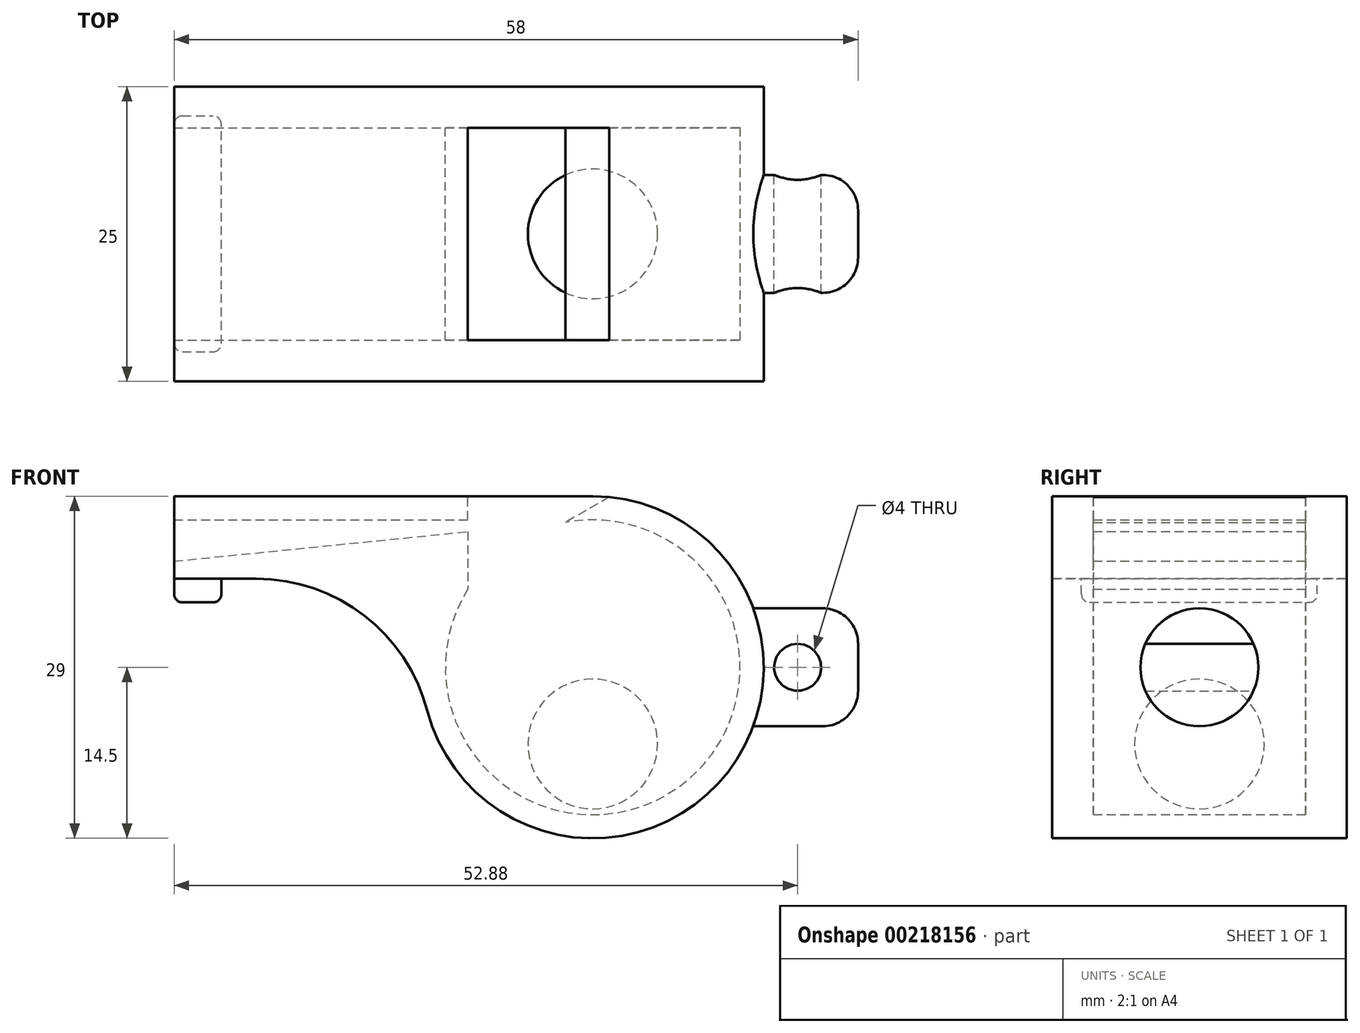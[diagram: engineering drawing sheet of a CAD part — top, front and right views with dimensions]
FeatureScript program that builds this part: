
annotation { "Feature Type Name" : "Feature", "Feature Type Description" : "" }
export const myFeature = defineFeature(function(context is Context, id is Id, definition is map)
    precondition{}
    {
        {
            var Q0;
            Q0=qCreatedBy(makeId("Front.planeOp"),FACE);
            var sketch = newSketch(context, id + "F0", { "sketchPlane" : qUnion([Q0])});
            skLineSegment(sketch, "E0", {"start": v(-35.5, 9) * mm, "end": v(-35.5, 12.5) * mm});
            skLineSegment(sketch, "E1", {"start": v(-35.5, 12.5) * mm, "end": v(-10.59, 12.5) * mm});
            skLineSegment(sketch, "E2", {"start": v(-10.59, 12.5) * mm, "end": v(-10.59, 14.5) * mm});
            skLineSegment(sketch, "E3", {"start": v(-10.59, 14.5) * mm, "end": v(0, 14.5) * mm});
            skLineSegment(sketch, "E4", {"start": v(-35.5, 9) * mm, "end": v(-10.59, 11.5) * mm});
            skLineSegment(sketch, "E5", {"start": v(-10.59, 11.5) * mm, "end": v(-10.59, 6.64) * mm});
            skArc(sketch, "E6", {"start": v(-10.59, 6.64) * mm, "mid": v(7.04, -10.33) * mm, "end": v(-2.3, 12.29) * mm});
            skArc(sketch, "E7", {"start": v(1.41, 14.43) * mm, "mid": v(0.7, 14.48) * mm, "end": v(0, 14.5) * mm});
            skLineSegment(sketch, "E8", {"start": v(-35.5, 9) * mm, "end": v(-1.25, 12.44) * mm, "construction": true});
            skLineSegment(sketch, "E9", {"start": v(1.41, 14.43) * mm, "end": v(-2.3, 12.29) * mm});
            skArc(sketch, "E10", {"start": v(-12.4, 7.5) * mm, "mid": v(7.12, -12.63) * mm, "end": v(0, 14.5) * mm});
            skLineSegment(sketch, "E11.bottom", {"start": v(-35.5, 14.5) * mm, "end": v(0, 14.5) * mm});
            skLineSegment(sketch, "E11.top", {"start": v(-35.5, 7.5) * mm, "end": v(-12.4, 7.5) * mm});
            skLineSegment(sketch, "E11.left", {"start": v(-35.5, 14.5) * mm, "end": v(-35.5, 7.5) * mm});
            skLineSegment(sketch, "E12", {"start": v(-35.5, 12.5) * mm, "end": v(-35.5, 9) * mm});
            skSolve(sketch);
        }
        {
            var Q0;
            {var subQ1=sQuery(id+"F0.wireOp",EDGE,"E4");Q0=makeQuery(id+"F0.imprint","IMPRINT",FACE,{"disambiguationData":[TD([[makeQuery(id+"F0.imprint","IMPRINT",EDGE,{"derivedFrom":subQ1}),-1.0]])]});}
            var Q1;
            {var subQ0=sQuery(id+"F0.wireOp",EDGE,"E1");Q1=makeQuery(id+"F0.imprint","IMPRINT",FACE,{"disambiguationData":[TD([[makeQuery(id+"F0.imprint","IMPRINT",EDGE,{"derivedFrom":subQ0}),1.0]])]});}
            var Q2;
            Q2=makeQuery(id+"F0.imprint","IMPRINT",FACE,{"disambiguationData":[TD([[makeQuery(id+"F0.imprint","IMPRINT",EDGE,{"derivedFrom":sQuery(id+"F0.wireOp",EDGE,"E1")}),-1.0]])]});
            extrude(context, id + "F1", {"entities" : qUnion([Q0, Q1, Q2]), "depth" : 25 * mm, "offsetDistance" : 25 * mm, "symmetric" : true});
        }
        {
            var Q0;
            Q0=makeQuery(id+"F0.imprint","IMPRINT",FACE,{"disambiguationData":[TD([[makeQuery(id+"F0.imprint","IMPRINT",EDGE,{"derivedFrom":sQuery(id+"F0.wireOp",EDGE,"E1")}),-1.0]])]});
            extrude(context, id + "F2", {"entities" : qUnion([Q0]), "operationType" : NewBodyOperationType.REMOVE, "depth" : 18 * mm, "offsetDistance" : 25 * mm, "symmetric" : true});
        }
        {
            var Q0;
            Q0=qCreatedBy(makeId("Front.planeOp"),FACE);
            var sketch = newSketch(context, id + "F3", { "sketchPlane" : qUnion([Q0])});
            skArc(sketch, "E13", {"start": v(0, -1) * mm, "mid": v(-5.5, -6.5) * mm, "end": v(0, -12) * mm});
            skLineSegment(sketch, "E14", {"start": v(0, -1) * mm, "end": v(0, -12) * mm});
            skSolve(sketch);
        }
        {
            var Q0;
            Q0=makeQuery(id+"F3.imprint","IMPRINT",FACE,{"disambiguationData":[TD([[makeQuery(id+"F3.imprint","IMPRINT",EDGE,{"derivedFrom":sQuery(id+"F3.wireOp",EDGE,"E13")}),1.0]])]});
            var Q1;
            Q1=sQuery(id+"F3.wireOp",EDGE,"E14");
            revolve(context, id + "F4", {"entities" : qUnion([Q0]), "axis" : qUnion([Q1]), "revolveType" : RevolveType.FULL});
        }
        {
            var Q0;
            Q0=qCreatedBy(makeId("Front.planeOp"),FACE);
            var sketch = newSketch(context, id + "F5", { "sketchPlane" : qUnion([Q0])});
            skLineSegment(sketch, "E15.bottom", {"start": v(12.5, 5) * mm, "end": v(22.5, 5) * mm});
            skLineSegment(sketch, "E15.top", {"start": v(12.5, 0) * mm, "end": v(22.5, 0) * mm});
            skLineSegment(sketch, "E15.left", {"start": v(12.5, 5) * mm, "end": v(12.5, 0) * mm});
            skLineSegment(sketch, "E15.right", {"start": v(22.5, 5) * mm, "end": v(22.5, 0) * mm});
            skSolve(sketch);
        }
        {
            var Q0;
            Q0=makeQuery(id+"F5.imprint","IMPRINT",FACE,{"disambiguationData":[TD([[makeQuery(id+"F5.imprint","IMPRINT",EDGE,{"derivedFrom":sQuery(id+"F5.wireOp",EDGE,"E15.bottom")}),-1.0]])]});
            var Q1;
            Q1=sQuery(id+"F5.wireOp",EDGE,"E15.top");
            revolve(context, id + "F6", {"operationType" : NewBodyOperationType.ADD, "entities" : qUnion([Q0]), "axis" : qUnion([Q1]), "revolveType" : RevolveType.FULL});
        }
        {
            var Q0;
            Q0=makeQuery(id+"F6.opRevolve","SWEPT_EDGE",EDGE,{"disambiguationData":[OSD([sQuery(id+"F5.wireOp",EDGE,"E15.bottom"),sQuery(id+"F5.wireOp",EDGE,"E15.right")])]});
            fillet(context, id + "F7", {"entities" : qUnion([Q0]), "radius" : 3 * mm, "tangentPropagation" : true, "allowEdgeOverflow" : false});
        }
        {
            var Q0;
            Q0=qCreatedBy(makeId("Front.planeOp"),FACE);
            var sketch = newSketch(context, id + "F8", { "sketchPlane" : qUnion([Q0])});
            skCircle(sketch, "E16", {"center": v(17.38, 0) * mm, "radius": 2 * mm});
            skSolve(sketch);
        }
        {
            var Q0;
            Q0 = qSketchRegion(id + "F8", true);
            extrude(context, id + "F9", {"entities" : qUnion([Q0]), "operationType" : NewBodyOperationType.REMOVE, "endBound" : BoundingType.THROUGH_ALL, "depth" : 25 * mm, "offsetDistance" : 25 * mm, "hasSecondDirection" : true, "secondDirectionBound" : BoundingType.THROUGH_ALL, "secondDirectionOppositeDirection" : true, "secondDirectionDepth" : 25 * mm});
        }
        {
            var Q0;
            Q0=makeQuery(id+"F1.opExtrude","SWEPT_FACE",FACE,{"disambiguationData":[OSD([sQuery(id+"F0.wireOp",EDGE,"E11.top")])]});
            var sketch = newSketch(context, id + "F10", { "sketchPlane" : qUnion([Q0])});
            skLineSegment(sketch, "E17.bottom", {"start": v(-35.5, 10) * mm, "end": v(-31.5, 10) * mm});
            skLineSegment(sketch, "E17.top", {"start": v(-35.5, -10) * mm, "end": v(-31.5, -10) * mm});
            skLineSegment(sketch, "E17.left", {"start": v(-35.5, 10) * mm, "end": v(-35.5, -10) * mm});
            skLineSegment(sketch, "E17.right", {"start": v(-31.5, 10) * mm, "end": v(-31.5, -10) * mm});
            skSolve(sketch);
        }
        {
            var Q0;
            Q0=makeQuery(id+"F10.imprint","IMPRINT",FACE,{"disambiguationData":[TD([[makeQuery(id+"F10.imprint","IMPRINT",EDGE,{"derivedFrom":sQuery(id+"F10.wireOp",EDGE,"E17.bottom")}),-1.0]])]});
            extrude(context, id + "F11", {"entities" : qUnion([Q0]), "operationType" : NewBodyOperationType.ADD, "depth" : 2 * mm, "offsetDistance" : 25 * mm});
        }
        {
            var Q0;
            Q0=makeQuery(id+"F11.opExtrude","CAP_FACE",FACE,{"disambiguationData":[OSD([sQuery(id+"F10.wireOp",EDGE,"E17.bottom"),sQuery(id+"F10.wireOp",EDGE,"E17.top"),sQuery(id+"F10.wireOp",EDGE,"E17.left"),sQuery(id+"F10.wireOp",EDGE,"E17.right")])],"isStart":false});
            var Q1;
            Q1=makeQuery(id+"F11.opExtrude","CAP_EDGE",EDGE,{"disambiguationData":[OSD([sQuery(id+"F10.wireOp",EDGE,"E17.bottom")])],"isStart":true});
            var Q2;
            Q2=makeQuery(id+"F11.opExtrude","CAP_EDGE",EDGE,{"disambiguationData":[OSD([sQuery(id+"F10.wireOp",EDGE,"E17.right")])],"isStart":true});
            var Q3;
            Q3=makeQuery(id+"F11.opExtrude","SWEPT_EDGE",EDGE,{"disambiguationData":[OSD([sQuery(id+"F10.wireOp",EDGE,"E17.bottom"),sQuery(id+"F10.wireOp",EDGE,"E17.right")])]});
            var Q4;
            Q4=makeQuery(id+"F11.opExtrude","SWEPT_EDGE",EDGE,{"disambiguationData":[OSD([sQuery(id+"F0.wireOp",EDGE,"E11.top"),sQuery(id+"F0.wireOp",EDGE,"E11.left"),sQuery(id+"F10.wireOp",EDGE,"E17.bottom"),sQuery(id+"F10.wireOp",EDGE,"E17.left")])]});
            var Q5;
            Q5=makeQuery(id+"F11.opExtrude","SWEPT_EDGE",EDGE,{"disambiguationData":[OSD([sQuery(id+"F0.wireOp",EDGE,"E11.top"),sQuery(id+"F0.wireOp",EDGE,"E11.left"),sQuery(id+"F10.wireOp",EDGE,"E17.top"),sQuery(id+"F10.wireOp",EDGE,"E17.left")])]});
            var Q6;
            Q6=makeQuery(id+"F11.opExtrude","CAP_EDGE",EDGE,{"disambiguationData":[OSD([sQuery(id+"F10.wireOp",EDGE,"E17.top")])],"isStart":true});
            var Q7;
            Q7=makeQuery(id+"F11.opExtrude","SWEPT_EDGE",EDGE,{"disambiguationData":[OSD([sQuery(id+"F10.wireOp",EDGE,"E17.top"),sQuery(id+"F10.wireOp",EDGE,"E17.right")])]});
            fillet(context, id + "F12", {"entities" : qUnion([Q0, Q1, Q2, Q3, Q4, Q5, Q6, Q7]), "radius" : 0.7 * mm, "tangentPropagation" : true, "allowEdgeOverflow" : false});
        }
        {
            var Q0;
            Q0=makeQuery(id+"F1.opExtrude","SWEPT_EDGE",EDGE,{"disambiguationData":[OSD([sQuery(id+"F0.wireOp",EDGE,"E10"),sQuery(id+"F0.wireOp",EDGE,"E11.top")])]});
            fillet(context, id + "F13", {"entities" : qUnion([Q0]), "radius" : 15 * mm, "tangentPropagation" : true, "allowEdgeOverflow" : false});
        }
    });
